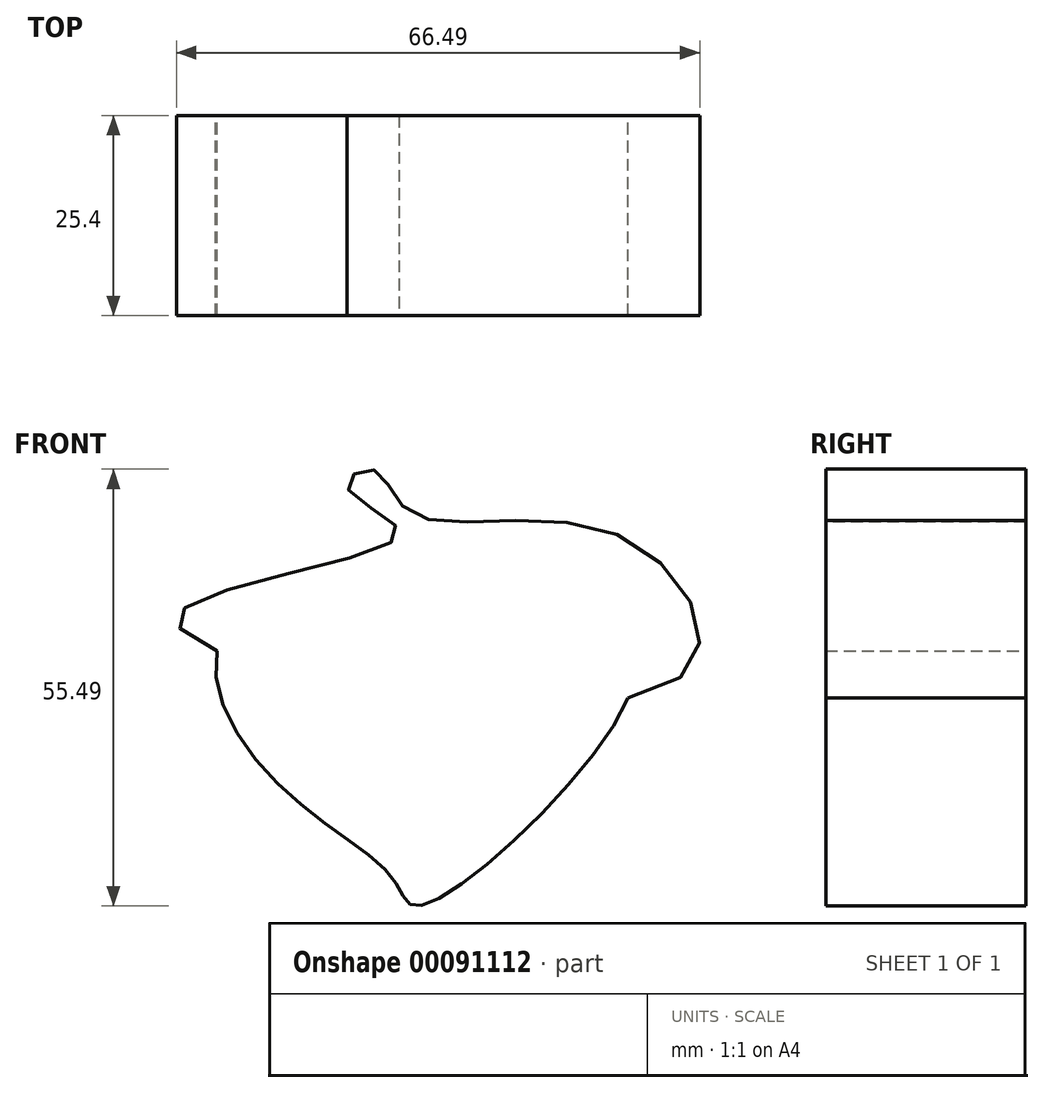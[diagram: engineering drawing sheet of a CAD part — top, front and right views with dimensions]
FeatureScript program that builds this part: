
annotation { "Feature Type Name" : "Feature", "Feature Type Description" : "" }
export const myFeature = defineFeature(function(context is Context, id is Id, definition is map)
    precondition{}
    {
        {
            var Q0;
            Q0=qCreatedBy(makeId("Front.planeOp"),FACE);
            var sketch = newSketch(context, id + "F0", { "sketchPlane" : qUnion([Q0])});
            skFitSpline(sketch, "E0", {"points": [v(13.16, 45.6) * mm, v(17.09, 25.98) * mm, v(33.02, 12.58) * mm, v(35.8, 9.12) * mm, v(56.57, 25.98) * mm, v(61.42, 45.6) * mm, v(13.16, 45.6) * mm]});
            skFitSpline(sketch, "E1", {"points": [v(27.25, 62.23) * mm, v(30.48, 64.54) * mm, v(35.33, 59) * mm, v(62.11, 56) * mm, v(69.04, 37.75) * mm, v(5.54, 45.6) * mm, v(33.71, 56.23) * mm, v(27.25, 62.23) * mm]});
            skSolve(sketch);
        }
        {
            var Q0;
            Q0 = qSketchRegion(id + "F0", true);
            extrude(context, id + "F1", {"entities" : qUnion([Q0]), "depth" : 25.4 * mm});
        }
    });
